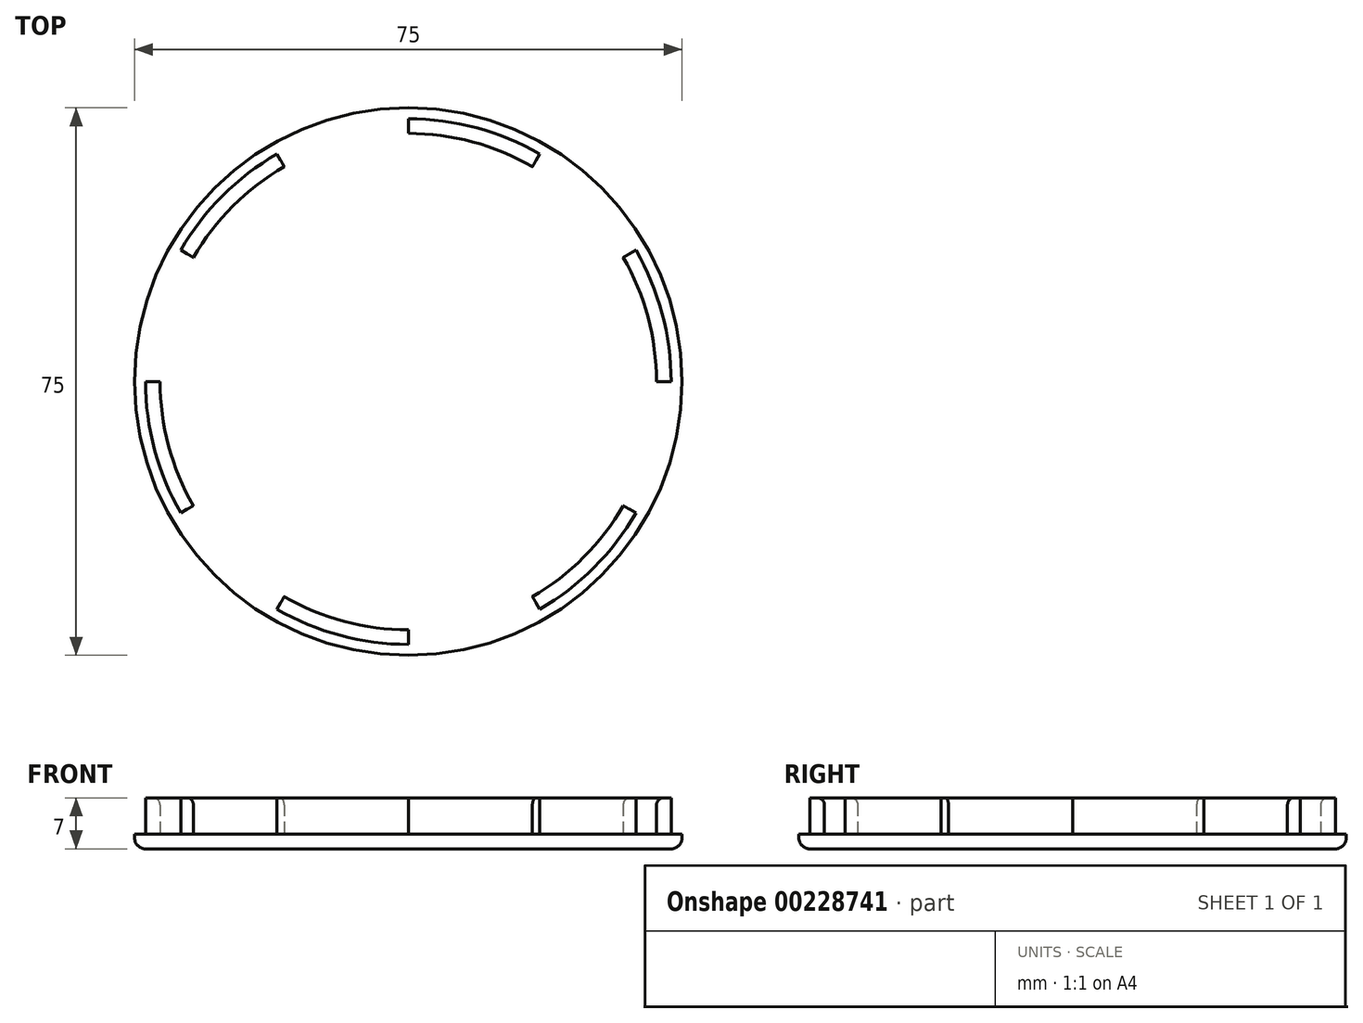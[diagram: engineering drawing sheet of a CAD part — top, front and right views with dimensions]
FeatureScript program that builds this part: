
annotation { "Feature Type Name" : "Feature", "Feature Type Description" : "" }
export const myFeature = defineFeature(function(context is Context, id is Id, definition is map)
    precondition{}
    {
        {
            var Q0;
            Q0=qCreatedBy(makeId("Top.planeOp"),FACE);
            var sketch = newSketch(context, id + "F0", { "sketchPlane" : qUnion([Q0])});
            skCircle(sketch, "E0", {"center": v(0, 0) * mm, "radius": 36 * mm});
            skCircle(sketch, "E1", {"center": v(0, 0) * mm, "radius": 37.5 * mm});
            skArc(sketch, "E2", {"start": v(-17, 29.44) * mm, "mid": v(-24.04, 24.04) * mm, "end": v(-29.44, 17) * mm});
            skLineSegment(sketch, "E3", {"start": v(0, 36) * mm, "end": v(0, -36) * mm, "construction": true});
            skLineSegment(sketch, "E4", {"start": v(-36, 0) * mm, "end": v(36, 0) * mm, "construction": true});
            skLineSegment(sketch, "E5", {"start": v(-18, 31.18) * mm, "end": v(18, -31.18) * mm, "construction": true});
            skLineSegment(sketch, "E6", {"start": v(-31.18, -18) * mm, "end": v(31.18, 18) * mm, "construction": true});
            skLineSegment(sketch, "E7", {"start": v(-31.18, 18) * mm, "end": v(31.18, -18) * mm, "construction": true});
            skLineSegment(sketch, "E8", {"start": v(-18, -31.18) * mm, "end": v(18, 31.18) * mm, "construction": true});
            skArc(sketch, "E9.trimOffspring", {"start": v(-34, 0) * mm, "mid": v(-32.84, -8.8) * mm, "end": v(-29.44, -17) * mm});
            skArc(sketch, "E10.trimOffspring", {"start": v(-17, -29.44) * mm, "mid": v(-8.8, -32.84) * mm, "end": v(0, -34) * mm});
            skArc(sketch, "E11.trimOffspring", {"start": v(17, -29.44) * mm, "mid": v(24.04, -24.04) * mm, "end": v(29.44, -17) * mm});
            skArc(sketch, "E12.trimOffspring", {"start": v(34, 0) * mm, "mid": v(32.84, 8.8) * mm, "end": v(29.44, 17) * mm});
            skArc(sketch, "E13.trimOffspring", {"start": v(17, 29.44) * mm, "mid": v(8.8, 32.84) * mm, "end": v(0, 34) * mm});
            skLineSegment(sketch, "E14", {"start": v(-17, 29.44) * mm, "end": v(-18, 31.18) * mm});
            skLineSegment(sketch, "E15", {"start": v(-29.44, 17) * mm, "end": v(-31.18, 18) * mm});
            skLineSegment(sketch, "E16", {"start": v(-36, 0) * mm, "end": v(-34, 0) * mm});
            skLineSegment(sketch, "E17", {"start": v(-29.44, -17) * mm, "end": v(-31.18, -18) * mm});
            skLineSegment(sketch, "E18", {"start": v(-18, -31.18) * mm, "end": v(-17, -29.44) * mm});
            skLineSegment(sketch, "E19", {"start": v(0, -34) * mm, "end": v(0, -36) * mm});
            skLineSegment(sketch, "E20", {"start": v(17, -29.44) * mm, "end": v(18, -31.18) * mm});
            skLineSegment(sketch, "E21", {"start": v(29.44, -17) * mm, "end": v(31.18, -18) * mm});
            skLineSegment(sketch, "E22", {"start": v(34, 0) * mm, "end": v(36, 0) * mm});
            skLineSegment(sketch, "E23", {"start": v(31.18, 18) * mm, "end": v(29.44, 17) * mm});
            skLineSegment(sketch, "E24", {"start": v(18, 31.18) * mm, "end": v(17, 29.44) * mm});
            skLineSegment(sketch, "E25", {"start": v(0, 36) * mm, "end": v(0, 34) * mm});
            skCircle(sketch, "E26", {"center": v(0, 0) * mm, "radius": 32 * mm});
            skSolve(sketch);
        }
        {
            var Q0;
            Q0=makeQuery(id+"F0.imprint","IMPRINT",FACE,{"disambiguationData":[TD([[makeQuery(id+"F0.imprint","IMPRINT",EDGE,{"derivedFrom":sQuery(id+"F0.wireOp",EDGE,"E0")}),1.0]])]});
            var Q1;
            Q1=makeQuery(id+"F0.imprint","IMPRINT",FACE,{"disambiguationData":[TD([[makeQuery(id+"F0.imprint","IMPRINT",EDGE,{"derivedFrom":sQuery(id+"F0.wireOp",EDGE,"E1")}),1.0]])]});
            var Q2;
            Q2=makeQuery(id+"F0.imprint","IMPRINT",FACE,{"disambiguationData":[TD([[makeQuery(id+"F0.imprint","IMPRINT",EDGE,{"derivedFrom":sQuery(id+"F0.wireOp",EDGE,"E26")}),1.0]])]});
            extrude(context, id + "F1", {"entities" : qUnion([Q0, Q1, Q2]), "depth" : 2 * mm});
        }
        {
            var Q0;
            Q0=makeQuery(id+"F0.imprint","IMPRINT",FACE,{"disambiguationData":[TD([[makeQuery(id+"F0.imprint","IMPRINT",EDGE,{"derivedFrom":sQuery(id+"F0.wireOp",EDGE,"E13.trimOffspring")}),-1.0]])]});
            var Q1;
            Q1=makeQuery(id+"F0.imprint","IMPRINT",FACE,{"disambiguationData":[TD([[makeQuery(id+"F0.imprint","IMPRINT",EDGE,{"derivedFrom":sQuery(id+"F0.wireOp",EDGE,"E12.trimOffspring")}),-1.0]])]});
            var Q2;
            Q2=makeQuery(id+"F0.imprint","IMPRINT",FACE,{"disambiguationData":[TD([[makeQuery(id+"F0.imprint","IMPRINT",EDGE,{"derivedFrom":sQuery(id+"F0.wireOp",EDGE,"E9.trimOffspring")}),-1.0]])]});
            var Q3;
            Q3=makeQuery(id+"F0.imprint","IMPRINT",FACE,{"disambiguationData":[TD([[makeQuery(id+"F0.imprint","IMPRINT",EDGE,{"derivedFrom":sQuery(id+"F0.wireOp",EDGE,"E11.trimOffspring")}),-1.0]])]});
            var Q4;
            Q4=makeQuery(id+"F0.imprint","IMPRINT",FACE,{"disambiguationData":[TD([[makeQuery(id+"F0.imprint","IMPRINT",EDGE,{"derivedFrom":sQuery(id+"F0.wireOp",EDGE,"E10.trimOffspring")}),-1.0]])]});
            var Q5;
            Q5=makeQuery(id+"F0.imprint","IMPRINT",FACE,{"disambiguationData":[TD([[makeQuery(id+"F0.imprint","IMPRINT",EDGE,{"derivedFrom":sQuery(id+"F0.wireOp",EDGE,"E2")}),-1.0]])]});
            extrude(context, id + "F2", {"entities" : qUnion([Q0, Q1, Q2, Q3, Q4, Q5]), "operationType" : NewBodyOperationType.ADD, "depth" : 7 * mm});
        }
        {
            var Q0;
            {var subQ0=sQuery(id+"F0.wireOp",EDGE,"E21");var subQ1=sQuery(id+"F0.wireOp",EDGE,"E20");var subQ2=sQuery(id+"F0.wireOp",EDGE,"E11.trimOffspring");var subQ3=sQuery(id+"F0.wireOp",EDGE,"E0");var subQ4=sQuery(id+"F0.wireOp",EDGE,"E19");var subQ5=sQuery(id+"F0.wireOp",EDGE,"E18");var subQ6=sQuery(id+"F0.wireOp",EDGE,"E10.trimOffspring");var subQ7=sQuery(id+"F0.wireOp",EDGE,"E17");var subQ8=sQuery(id+"F0.wireOp",EDGE,"E16");var subQ9=sQuery(id+"F0.wireOp",EDGE,"E9.trimOffspring");var subQ10=sQuery(id+"F0.wireOp",EDGE,"E15");var subQ11=sQuery(id+"F0.wireOp",EDGE,"E14");var subQ12=sQuery(id+"F0.wireOp",EDGE,"E2");var subQ13=sQuery(id+"F0.wireOp",EDGE,"E25");var subQ14=sQuery(id+"F0.wireOp",EDGE,"E24");var subQ15=sQuery(id+"F0.wireOp",EDGE,"E13.trimOffspring");var subQ16=sQuery(id+"F0.wireOp",EDGE,"E23");var subQ17=sQuery(id+"F0.wireOp",EDGE,"E22");var subQ18=sQuery(id+"F0.wireOp",EDGE,"E12.trimOffspring");Q0=makeQuery(id+"F2.boolean.opBoolean","MERGE",FACE,{"derivedFrom":[makeQuery(id+"F1.opExtrude","CAP_FACE",FACE,{"disambiguationData":[OSD([subQ3,sQuery(id+"F0.wireOp",EDGE,"E1"),subQ12,subQ9,subQ6,subQ2,subQ18,subQ15,subQ11,subQ10,subQ8,subQ7,subQ5,subQ4,subQ1,subQ0,subQ17,subQ16,subQ14,subQ13])],"isStart":true}),makeQuery(id+"F2.opExtrude","CAP_FACE",FACE,{"disambiguationData":[OSD([subQ3,subQ18,subQ17,subQ16])],"isStart":true}),makeQuery(id+"F2.opExtrude","CAP_FACE",FACE,{"disambiguationData":[OSD([subQ3,subQ15,subQ14,subQ13])],"isStart":true}),makeQuery(id+"F2.opExtrude","CAP_FACE",FACE,{"disambiguationData":[OSD([subQ3,subQ12,subQ11,subQ10])],"isStart":true}),makeQuery(id+"F2.opExtrude","CAP_FACE",FACE,{"disambiguationData":[OSD([subQ3,subQ9,subQ8,subQ7])],"isStart":true}),makeQuery(id+"F2.opExtrude","CAP_FACE",FACE,{"disambiguationData":[OSD([subQ3,subQ6,subQ5,subQ4])],"isStart":true}),makeQuery(id+"F2.opExtrude","CAP_FACE",FACE,{"disambiguationData":[OSD([subQ3,subQ2,subQ1,subQ0])],"isStart":true})]});}
            fillet(context, id + "F3", {"entities" : qUnion([Q0]), "radius" : 1.5 * mm, "tangentPropagation" : true, "allowEdgeOverflow" : false});
        }
        {
            var Q0;
            Q0=makeQuery(id+"F2.opExtrude","CAP_EDGE",EDGE,{"disambiguationData":[OSD([sQuery(id+"F0.wireOp",EDGE,"E2")])],"isStart":false});
            var Q1;
            Q1=makeQuery(id+"F2.opExtrude","CAP_EDGE",EDGE,{"disambiguationData":[OSD([sQuery(id+"F0.wireOp",EDGE,"E13.trimOffspring")])],"isStart":false});
            var Q2;
            Q2=makeQuery(id+"F2.opExtrude","CAP_EDGE",EDGE,{"disambiguationData":[OSD([sQuery(id+"F0.wireOp",EDGE,"E12.trimOffspring")])],"isStart":false});
            var Q3;
            Q3=makeQuery(id+"F2.opExtrude","CAP_EDGE",EDGE,{"disambiguationData":[OSD([sQuery(id+"F0.wireOp",EDGE,"E11.trimOffspring")])],"isStart":false});
            var Q4;
            Q4=makeQuery(id+"F2.opExtrude","CAP_EDGE",EDGE,{"disambiguationData":[OSD([sQuery(id+"F0.wireOp",EDGE,"E10.trimOffspring")])],"isStart":false});
            var Q5;
            Q5=makeQuery(id+"F2.opExtrude","CAP_EDGE",EDGE,{"disambiguationData":[OSD([sQuery(id+"F0.wireOp",EDGE,"E9.trimOffspring")])],"isStart":false});
            var Q6;
            Q6=makeQuery(id+"F1.opExtrude","CAP_EDGE",EDGE,{"disambiguationData":[OSD([sQuery(id+"F0.wireOp",EDGE,"E2")])],"isStart":false});
            var Q7;
            Q7=makeQuery(id+"F1.opExtrude","CAP_EDGE",EDGE,{"disambiguationData":[OSD([sQuery(id+"F0.wireOp",EDGE,"E13.trimOffspring")])],"isStart":false});
            var Q8;
            Q8=makeQuery(id+"F1.opExtrude","CAP_EDGE",EDGE,{"disambiguationData":[OSD([sQuery(id+"F0.wireOp",EDGE,"E12.trimOffspring")])],"isStart":false});
            var Q9;
            Q9=makeQuery(id+"F1.opExtrude","CAP_EDGE",EDGE,{"disambiguationData":[OSD([sQuery(id+"F0.wireOp",EDGE,"E9.trimOffspring")])],"isStart":false});
            var Q10;
            Q10=makeQuery(id+"F1.opExtrude","CAP_EDGE",EDGE,{"disambiguationData":[OSD([sQuery(id+"F0.wireOp",EDGE,"E10.trimOffspring")])],"isStart":false});
            var Q11;
            Q11=makeQuery(id+"F1.opExtrude","CAP_EDGE",EDGE,{"disambiguationData":[OSD([sQuery(id+"F0.wireOp",EDGE,"E11.trimOffspring")])],"isStart":false});
            var Q12;
            Q12=makeQuery(id+"F1.opExtrude","CAP_EDGE",EDGE,{"disambiguationData":[OSD([sQuery(id+"F0.wireOp",EDGE,"E19")])],"isStart":false});
            var Q13;
            Q13=makeQuery(id+"F1.opExtrude","CAP_EDGE",EDGE,{"disambiguationData":[OSD([sQuery(id+"F0.wireOp",EDGE,"E17")])],"isStart":false});
            var Q14;
            Q14=makeQuery(id+"F1.opExtrude","CAP_EDGE",EDGE,{"disambiguationData":[OSD([sQuery(id+"F0.wireOp",EDGE,"E22")])],"isStart":false});
            var Q15;
            Q15=makeQuery(id+"F1.opExtrude","CAP_EDGE",EDGE,{"disambiguationData":[OSD([sQuery(id+"F0.wireOp",EDGE,"E24")])],"isStart":false});
            var Q16;
            Q16=makeQuery(id+"F1.opExtrude","CAP_EDGE",EDGE,{"disambiguationData":[OSD([sQuery(id+"F0.wireOp",EDGE,"E21")])],"isStart":false});
            var Q17;
            Q17=makeQuery(id+"F1.opExtrude","CAP_EDGE",EDGE,{"disambiguationData":[OSD([sQuery(id+"F0.wireOp",EDGE,"E20")])],"isStart":false});
            var Q18;
            Q18=makeQuery(id+"F1.opExtrude","CAP_EDGE",EDGE,{"disambiguationData":[OSD([sQuery(id+"F0.wireOp",EDGE,"E14")])],"isStart":false});
            var Q19;
            Q19=makeQuery(id+"F1.opExtrude","CAP_EDGE",EDGE,{"disambiguationData":[OSD([sQuery(id+"F0.wireOp",EDGE,"E16")])],"isStart":false});
            var Q20;
            Q20=makeQuery(id+"F1.opExtrude","CAP_EDGE",EDGE,{"disambiguationData":[OSD([sQuery(id+"F0.wireOp",EDGE,"E25")])],"isStart":false});
            var Q21;
            Q21=makeQuery(id+"F1.opExtrude","CAP_EDGE",EDGE,{"disambiguationData":[OSD([sQuery(id+"F0.wireOp",EDGE,"E18")])],"isStart":false});
            var Q22;
            Q22=makeQuery(id+"F1.opExtrude","CAP_EDGE",EDGE,{"disambiguationData":[OSD([sQuery(id+"F0.wireOp",EDGE,"E15")])],"isStart":false});
            var Q23;
            Q23=makeQuery(id+"F1.opExtrude","CAP_EDGE",EDGE,{"disambiguationData":[OSD([sQuery(id+"F0.wireOp",EDGE,"E23")])],"isStart":false});
            fillet(context, id + "F4", {"entities" : qUnion([Q0, Q1, Q2, Q3, Q4, Q5, Q6, Q7, Q8, Q9, Q10, Q11, Q12, Q13, Q14, Q15, Q16, Q17, Q18, Q19, Q20, Q21, Q22, Q23]), "radius" : 1 * mm, "tangentPropagation" : true, "allowEdgeOverflow" : false});
        }
    });
